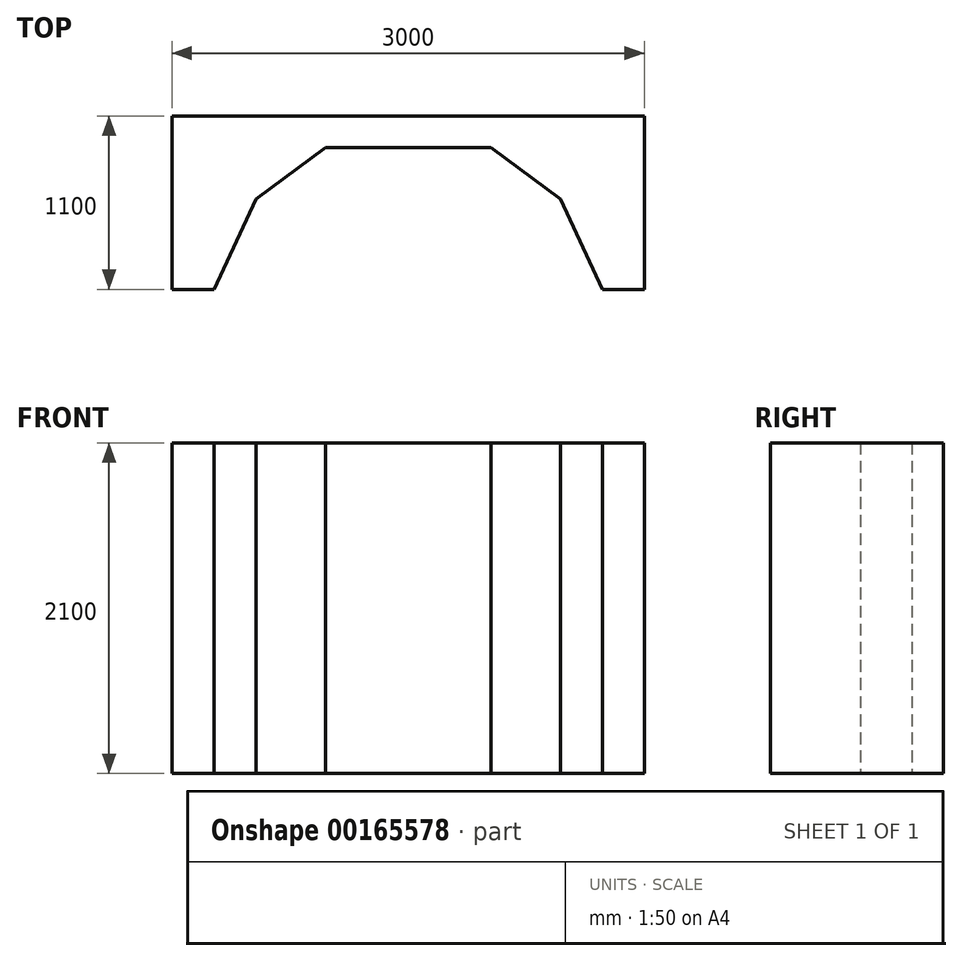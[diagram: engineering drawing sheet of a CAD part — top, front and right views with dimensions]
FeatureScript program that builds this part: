
annotation { "Feature Type Name" : "Feature", "Feature Type Description" : "" }
export const myFeature = defineFeature(function(context is Context, id is Id, definition is map)
    precondition{}
    {
        {
            var Q0;
            Q0=qCreatedBy(makeId("Top.planeOp"),FACE);
            var sketch = newSketch(context, id + "F0", { "sketchPlane" : qUnion([Q0])});
            skLineSegment(sketch, "E0", {"start": v(-525, 0) * mm, "end": v(525, 0) * mm});
            skLineSegment(sketch, "E1", {"start": v(525, 0) * mm, "end": v(967.3, -326.9) * mm});
            skLineSegment(sketch, "E2", {"start": v(967.3, -326.9) * mm, "end": v(1233.67, -900) * mm});
            skLineSegment(sketch, "E3", {"start": v(-1233.67, -900) * mm, "end": v(-967.3, -326.9) * mm});
            skLineSegment(sketch, "E4", {"start": v(-967.3, -326.9) * mm, "end": v(-525, 0) * mm});
            skLineSegment(sketch, "E5", {"start": v(1500, -900) * mm, "end": v(1233.67, -900) * mm});
            skLineSegment(sketch, "E6", {"start": v(1500, -900) * mm, "end": v(1500, 200) * mm});
            skLineSegment(sketch, "E7", {"start": v(1500, 200) * mm, "end": v(-1500, 200) * mm});
            skLineSegment(sketch, "E8", {"start": v(-1500, 200) * mm, "end": v(-1500, -900) * mm});
            skLineSegment(sketch, "E9", {"start": v(-1500, -900) * mm, "end": v(-1233.67, -900) * mm});
            skPoint(sketch, "E10", {"position": v(0, 0) * mm});
            skPoint(sketch, "E11", {"position": v(0, 200) * mm});
            skSolve(sketch);
        }
        {
            var Q0;
            Q0=makeQuery(id+"F0.imprint","IMPRINT",FACE,{"disambiguationData":[TD([[makeQuery(id+"F0.imprint","IMPRINT",EDGE,{"derivedFrom":sQuery(id+"F0.wireOp",EDGE,"E0")}),1.0]])]});
            extrude(context, id + "F1", {"entities" : qUnion([Q0]), "depth" : 2100 * mm});
        }
    });
